# Revit family: IS_Connect_Multiproduct_BIM_NL_E7127;E7128
name_source: partatom
category: Plumbing Fixtures
revit_build: Autodesk Revit MEP 2014 (Build: 20130308_1515(x64)
units: mm (PartAtom-declared; Revit-internal decimal feet)

## types (2) — shared parameters
Accessories = www.idealstandardnederland.nl
AreaUnits = millimeters
Assembly Code = C1030200
AssetType = Vast
BREEAMApproved = No
Brand = Ideal Standard
ConnectionType = Sanitair
DurationUnit = jaar
ECA = No
ExpectedLife = 25
Finish = Wit
IfcExportAs = IfcSanitaryTerminalType
IfcExportType = Closetzitting
InstallationInstructions = http://www.idealstandardnederland.nl
LinearUnits = millimeters
ManufacturerURL = www.idealstandardnederland.nl
NominalHeight = 45 mm
NominalLength = 435 mm
NominalWidth = 368 mm
PanColor = Wit
PanMaterial = Duroplast
ProductInformation = http://www.idealstandardnederland.nl
Shape = Gesculptuurd
Size = 368 x 435 x 45 mm
Space = Internal
URL = www.idealstandardnederland.nl
Version = 1
VolumeUnits = liter
WRAS = No
WarrantyDescription = Fabrieksgarantie
WarrantyDurationParts = 5
WarrantyDurationUnit = jaar
WaterEfficientProduct = No
zero-valued in all types: CWFU, Cost, Default Elevation, HWFU, SpilloverLevel, WFU

## per-type parameters (varying)
| type | BIMObjectName | BarCode | Description | Features | Model | ModelNumber | ModelReference | NBSDescription | NBSReference | Name | NettWeight |
| E712801 - CONNECT ZITTING & DEKSEL NORMAL CLOSE | ISI_IdealStandard_WcPans_E712801 | 5017830399391 | Connect zitting en deksel, duroplast, RVS scharnieren. | Zitting en deksel, duroplast, RVS scharnieren. | E712801 | E712801 | Connect zitting en deksel, duroplast, RVS scharnieren. | WC seats and covers | 45-35-70/391 | WcPans_E712801_IdealStandard | 2.5 kg |
| E712701 - CONNECT ZITTING & DEKSEL SOFT CLOSE | ISI_IdealStandard_WcPans_E712701 | 5017830399414 | Connect zitting en deksel softclosing, duroplast, RVS scharnieren (easy take off). | Zitting en deksel softclosing, duroplast, RVS scharnieren (easy take off). | E712701 | E712701 | Connect zitting en deksel softclosing, duroplast, RVS scharnieren (easy take off). | WC seat | 45-30-70/384 | WcPans_E712701_IdealStandard | 3 kg |

## geometry (parser evidence)
native form markers: Sweep x2
no freeform markers — native parametric forms only
